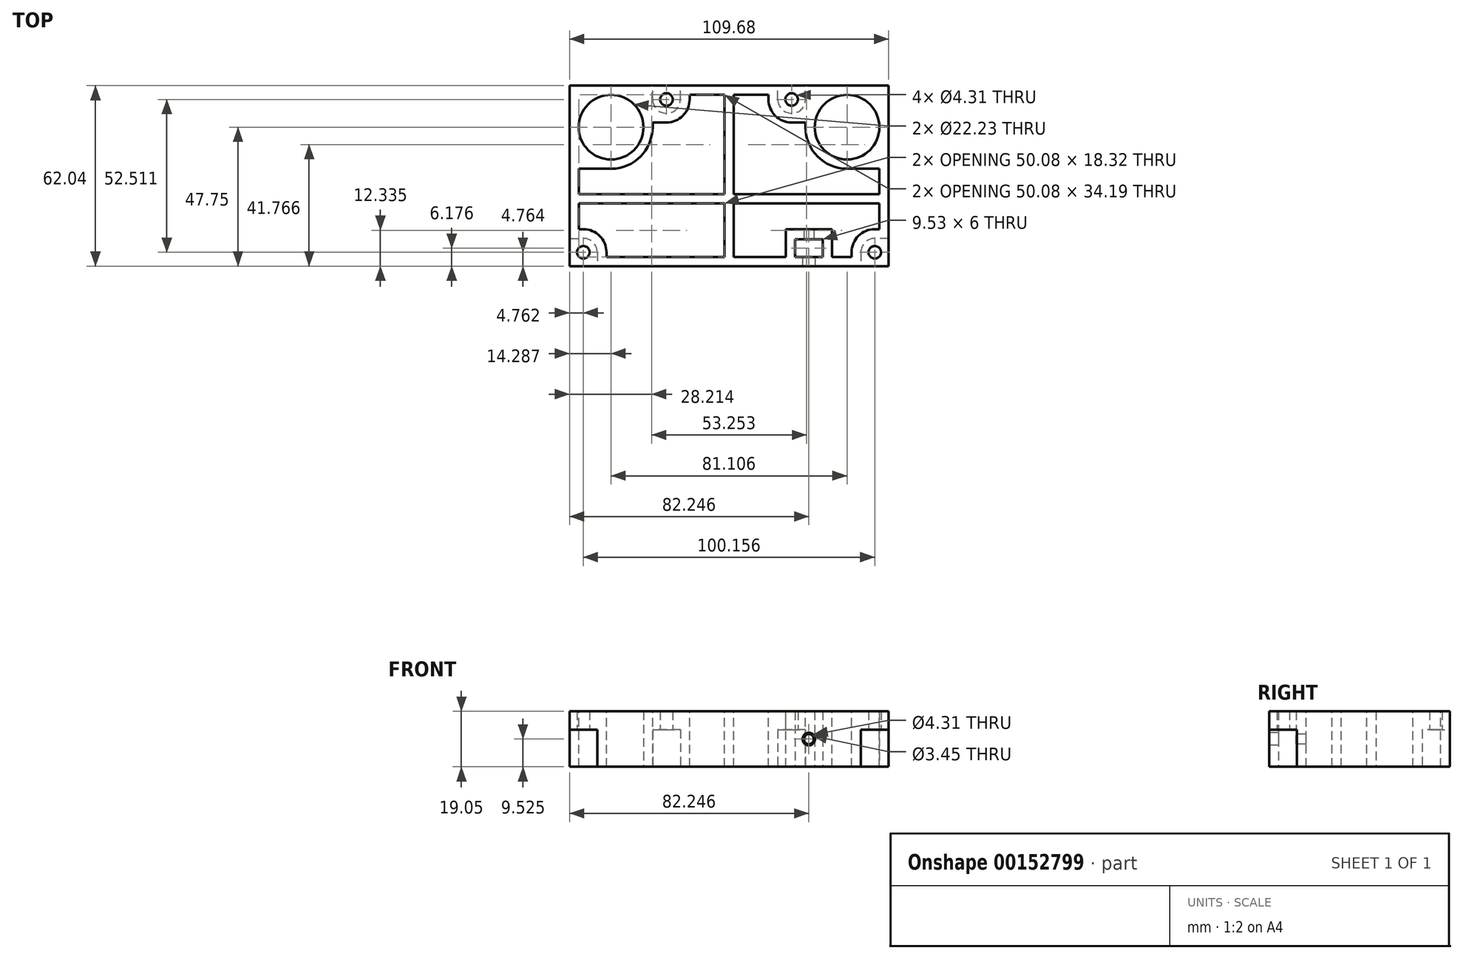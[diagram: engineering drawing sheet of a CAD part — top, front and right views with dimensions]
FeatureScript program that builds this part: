
annotation { "Feature Type Name" : "Feature", "Feature Type Description" : "" }
export const myFeature = defineFeature(function(context is Context, id is Id, definition is map)
    precondition{}
    {
        {
            var Q0;
            Q0=qCreatedBy(makeId("Top.planeOp"),FACE);
            var sketch = newSketch(context, id + "F0", { "sketchPlane" : qUnion([Q0])});
            skLineSegment(sketch, "E0.bottom", {"start": v(-40.55, 0) * mm, "end": v(40.55, 0) * mm, "construction": true});
            skPoint(sketch, "E0.middle", {"position": v(0, 0) * mm});
            skLineSegment(sketch, "E1", {"start": v(-40.55, 0) * mm, "end": v(-40.55, 14.29) * mm, "construction": true});
            skLineSegment(sketch, "E2", {"start": v(-40.55, 0) * mm, "end": v(-54.84, 0) * mm, "construction": true});
            skCircle(sketch, "E3", {"center": v(-40.55, 0) * mm, "radius": 11.11 * mm});
            skCircle(sketch, "E4", {"center": v(40.55, 0) * mm, "radius": 11.11 * mm});
            skLineSegment(sketch, "E5.bottom", {"start": v(-54.84, 14.29) * mm, "end": v(54.84, 14.29) * mm});
            skLineSegment(sketch, "E5.top", {"start": v(-54.84, -47.75) * mm, "end": v(54.84, -47.75) * mm});
            skLineSegment(sketch, "E5.left", {"start": v(-54.84, 14.29) * mm, "end": v(-54.84, -47.75) * mm});
            skLineSegment(sketch, "E5.right", {"start": v(54.84, 14.29) * mm, "end": v(54.84, -47.75) * mm});
            skLineSegment(sketch, "E6", {"start": v(0, 0) * mm, "end": v(0, -41.57) * mm, "construction": true});
            skLineSegment(sketch, "E7", {"start": v(0, -41.57) * mm, "end": v(22.64, -41.57) * mm, "construction": true});
            skLineSegment(sketch, "E8.bottom", {"start": v(22.64, -38.57) * mm, "end": v(32.17, -38.57) * mm});
            skLineSegment(sketch, "E8.top", {"start": v(22.64, -44.57) * mm, "end": v(32.17, -44.57) * mm});
            skLineSegment(sketch, "E8.left", {"start": v(22.64, -38.57) * mm, "end": v(22.64, -44.57) * mm});
            skLineSegment(sketch, "E8.right", {"start": v(32.17, -38.57) * mm, "end": v(32.17, -44.57) * mm});
            skLineSegment(sketch, "E9", {"start": v(0, -41.57) * mm, "end": v(0, -47.75) * mm, "construction": true});
            skLineSegment(sketch, "E10", {"start": v(0, 0) * mm, "end": v(0, 9.53) * mm, "construction": true});
            skLineSegment(sketch, "E11", {"start": v(-21.5, 9.53) * mm, "end": v(21.5, 9.53) * mm, "construction": true});
            skLineSegment(sketch, "E12", {"start": v(-50.08, -47.75) * mm, "end": v(-50.08, -42.99) * mm, "construction": true});
            skLineSegment(sketch, "E13", {"start": v(-50.08, -42.99) * mm, "end": v(-54.84, -42.99) * mm, "construction": true});
            skLineSegment(sketch, "E14", {"start": v(54.84, -42.99) * mm, "end": v(50.08, -42.99) * mm, "construction": true});
            skCircle(sketch, "E15", {"center": v(-50.08, -42.99) * mm, "radius": 2.15 * mm});
            skCircle(sketch, "E16", {"center": v(50.08, -42.99) * mm, "radius": 2.15 * mm});
            skCircle(sketch, "E17", {"center": v(-21.5, 9.53) * mm, "radius": 2.15 * mm});
            skCircle(sketch, "E18", {"center": v(21.5, 9.53) * mm, "radius": 2.15 * mm});
            skSolve(sketch);
        }
        {
            var Q0;
            Q0=qSketchRegion(id+"F0",true);
            extrude(context, id + "F1", {"entities" : qUnion([Q0]), "depth" : 19.05 * mm});
        }
        {
            var Q0;
            Q0=makeQuery(id+"F1.opExtrude","CAP_FACE",FACE,{"disambiguationData":[OSD([sQuery(id+"F0.wireOp",EDGE,"E3"),sQuery(id+"F0.wireOp",EDGE,"E4"),sQuery(id+"F0.wireOp",EDGE,"E5.bottom"),sQuery(id+"F0.wireOp",EDGE,"E5.top"),sQuery(id+"F0.wireOp",EDGE,"E5.left"),sQuery(id+"F0.wireOp",EDGE,"E5.right"),sQuery(id+"F0.wireOp",EDGE,"E8.bottom"),sQuery(id+"F0.wireOp",EDGE,"E8.top"),sQuery(id+"F0.wireOp",EDGE,"E8.left"),sQuery(id+"F0.wireOp",EDGE,"E8.right"),sQuery(id+"F0.wireOp",EDGE,"E15"),sQuery(id+"F0.wireOp",EDGE,"E16"),sQuery(id+"F0.wireOp",EDGE,"E17"),sQuery(id+"F0.wireOp",EDGE,"E18")])],"isStart":true});
            var sketch = newSketch(context, id + "F2", { "sketchPlane" : qUnion([Q0])});
            skLineSegment(sketch, "E19.bottom", {"start": v(-26.27, -14.29) * mm, "end": v(-16.74, -14.29) * mm});
            skLineSegment(sketch, "E19.top", {"start": v(-26.27, -4.76) * mm, "end": v(-16.74, -4.76) * mm});
            skLineSegment(sketch, "E19.left", {"start": v(-16.74, -4.76) * mm, "end": v(-16.74, -14.29) * mm});
            skLineSegment(sketch, "E19.right", {"start": v(-26.27, -4.76) * mm, "end": v(-26.27, -14.29) * mm});
            skPoint(sketch, "E19.middle", {"position": v(-21.5, -9.53) * mm});
            skLineSegment(sketch, "E20.bottom", {"start": v(26.27, -14.29) * mm, "end": v(16.74, -14.29) * mm});
            skLineSegment(sketch, "E20.top", {"start": v(26.27, -4.76) * mm, "end": v(16.74, -4.76) * mm});
            skLineSegment(sketch, "E20.left", {"start": v(16.74, -4.76) * mm, "end": v(16.74, -14.29) * mm});
            skLineSegment(sketch, "E20.right", {"start": v(26.27, -4.76) * mm, "end": v(26.27, -14.29) * mm});
            skPoint(sketch, "E20.middle", {"position": v(21.5, -9.53) * mm});
            skLineSegment(sketch, "E21.bottom", {"start": v(54.84, 47.75) * mm, "end": v(45.32, 47.75) * mm});
            skLineSegment(sketch, "E21.top", {"start": v(54.84, 38.22) * mm, "end": v(45.32, 38.22) * mm});
            skLineSegment(sketch, "E21.left", {"start": v(54.84, 38.22) * mm, "end": v(54.84, 47.75) * mm});
            skLineSegment(sketch, "E21.right", {"start": v(45.32, 38.22) * mm, "end": v(45.32, 47.75) * mm});
            skPoint(sketch, "E21.middle", {"position": v(50.08, 42.99) * mm});
            skLineSegment(sketch, "E22.bottom", {"start": v(-54.84, 47.75) * mm, "end": v(-45.32, 47.75) * mm});
            skLineSegment(sketch, "E22.top", {"start": v(-54.84, 38.22) * mm, "end": v(-45.32, 38.22) * mm});
            skLineSegment(sketch, "E22.left", {"start": v(-54.84, 38.22) * mm, "end": v(-54.84, 47.75) * mm});
            skLineSegment(sketch, "E22.right", {"start": v(-45.32, 38.22) * mm, "end": v(-45.32, 47.75) * mm});
            skPoint(sketch, "E22.middle", {"position": v(-50.08, 42.99) * mm});
            skSolve(sketch);
        }
        {
            var Q0;
            Q0=qSketchRegion(id+"F2",true);
            extrude(context, id + "F3", {"entities" : qUnion([Q0]), "operationType" : NewBodyOperationType.REMOVE, "oppositeDirection" : true, "depth" : 12.7 * mm});
        }
        {
            var Q0;
            Q0=makeQuery(id+"F3.boolean.opBoolean","COPY",EDGE,{"derivedFrom":makeQuery(id+"F3.opExtrude","SWEPT_EDGE",EDGE,{"disambiguationData":[OSD([sQuery(id+"F2.wireOp",EDGE,"E22.top"),sQuery(id+"F2.wireOp",EDGE,"E22.right")])]})});
            var Q1;
            Q1=makeQuery(id+"F3.boolean.opBoolean","COPY",EDGE,{"derivedFrom":makeQuery(id+"F3.opExtrude","SWEPT_EDGE",EDGE,{"disambiguationData":[OSD([sQuery(id+"F2.wireOp",EDGE,"E21.top"),sQuery(id+"F2.wireOp",EDGE,"E21.right")])]})});
            var Q2;
            Q2=makeQuery(id+"F3.boolean.opBoolean","COPY",EDGE,{"derivedFrom":makeQuery(id+"F3.opExtrude","SWEPT_EDGE",EDGE,{"disambiguationData":[OSD([sQuery(id+"F2.wireOp",EDGE,"E20.top"),sQuery(id+"F2.wireOp",EDGE,"E20.right")])]})});
            var Q3;
            Q3=makeQuery(id+"F3.boolean.opBoolean","COPY",EDGE,{"derivedFrom":makeQuery(id+"F3.opExtrude","SWEPT_EDGE",EDGE,{"disambiguationData":[OSD([sQuery(id+"F2.wireOp",EDGE,"E20.top"),sQuery(id+"F2.wireOp",EDGE,"E20.left")])]})});
            var Q4;
            Q4=makeQuery(id+"F3.boolean.opBoolean","COPY",EDGE,{"derivedFrom":makeQuery(id+"F3.opExtrude","SWEPT_EDGE",EDGE,{"disambiguationData":[OSD([sQuery(id+"F2.wireOp",EDGE,"E19.top"),sQuery(id+"F2.wireOp",EDGE,"E19.right")])]})});
            var Q5;
            Q5=makeQuery(id+"F3.boolean.opBoolean","COPY",EDGE,{"derivedFrom":makeQuery(id+"F3.opExtrude","SWEPT_EDGE",EDGE,{"disambiguationData":[OSD([sQuery(id+"F2.wireOp",EDGE,"E19.top"),sQuery(id+"F2.wireOp",EDGE,"E19.left")])]})});
            fillet(context, id + "F4", {"entities" : qUnion([Q0, Q1, Q2, Q3, Q4, Q5]), "radius" : 4.76 * mm, "tangentPropagation" : true, "allowEdgeOverflow" : false});
        }
        {
            var Q0;
            Q0=makeQuery(id+"F1.opExtrude","CAP_FACE",FACE,{"disambiguationData":[OSD([sQuery(id+"F0.wireOp",EDGE,"E3"),sQuery(id+"F0.wireOp",EDGE,"E4"),sQuery(id+"F0.wireOp",EDGE,"E5.bottom"),sQuery(id+"F0.wireOp",EDGE,"E5.top"),sQuery(id+"F0.wireOp",EDGE,"E5.left"),sQuery(id+"F0.wireOp",EDGE,"E5.right"),sQuery(id+"F0.wireOp",EDGE,"E8.bottom"),sQuery(id+"F0.wireOp",EDGE,"E8.top"),sQuery(id+"F0.wireOp",EDGE,"E8.left"),sQuery(id+"F0.wireOp",EDGE,"E8.right"),sQuery(id+"F0.wireOp",EDGE,"E15"),sQuery(id+"F0.wireOp",EDGE,"E16"),sQuery(id+"F0.wireOp",EDGE,"E17"),sQuery(id+"F0.wireOp",EDGE,"E18")])],"isStart":false});
            var sketch = newSketch(context, id + "F5", { "sketchPlane" : qUnion([Q0])});
            skLineSegment(sketch, "E23.bottom", {"start": v(51.67, -23.08) * mm, "end": v(-51.67, -23.08) * mm});
            skLineSegment(sketch, "E23.top", {"start": v(51.67, -26.26) * mm, "end": v(-51.67, -26.26) * mm});
            skLineSegment(sketch, "E23.left", {"start": v(51.67, -23.08) * mm, "end": v(51.67, -26.26) * mm, "construction": true});
            skLineSegment(sketch, "E23.right", {"start": v(-51.67, -23.08) * mm, "end": v(-51.67, -26.26) * mm, "construction": true});
            skLineSegment(sketch, "E24.bottom", {"start": v(-1.59, -44.57) * mm, "end": v(1.59, -44.57) * mm, "construction": true});
            skLineSegment(sketch, "E24.top", {"start": v(-1.59, 11.11) * mm, "end": v(1.59, 11.11) * mm, "construction": true});
            skLineSegment(sketch, "E24.left", {"start": v(-1.59, -44.57) * mm, "end": v(-1.59, 11.11) * mm});
            skLineSegment(sketch, "E24.right", {"start": v(1.59, -44.57) * mm, "end": v(1.59, 11.11) * mm});
            skArc(sketch, "E25", {"start": v(-40.55, -14.29) * mm, "mid": v(-30.45, -10.1) * mm, "end": v(-26.27, 0) * mm});
            skArc(sketch, "E26", {"start": v(-21.5, 1.59) * mm, "mid": v(-15.9, 3.91) * mm, "end": v(-13.57, 9.53) * mm});
            skArc(sketch, "E27", {"start": v(13.57, 9.53) * mm, "mid": v(15.9, 3.91) * mm, "end": v(21.5, 1.59) * mm});
            skArc(sketch, "E28", {"start": v(26.27, 0) * mm, "mid": v(30.45, -10.1) * mm, "end": v(40.55, -14.29) * mm});
            skArc(sketch, "E29", {"start": v(50.08, -35.05) * mm, "mid": v(44.47, -37.37) * mm, "end": v(42.14, -42.99) * mm});
            skArc(sketch, "E30", {"start": v(-42.14, -42.99) * mm, "mid": v(-44.47, -37.37) * mm, "end": v(-50.08, -35.05) * mm});
            skLineSegment(sketch, "E31", {"start": v(27.4, -44.57) * mm, "end": v(27.4, -47.75) * mm, "construction": true});
            skLineSegment(sketch, "E32", {"start": v(27.4, -44.57) * mm, "end": v(27.4, -35.05) * mm, "construction": true});
            skLineSegment(sketch, "E33.bottom", {"start": v(19.47, -35.05) * mm, "end": v(35.34, -35.05) * mm});
            skLineSegment(sketch, "E33.left", {"start": v(19.47, -35.05) * mm, "end": v(19.47, -44.57) * mm});
            skLineSegment(sketch, "E33.right", {"start": v(35.34, -35.05) * mm, "end": v(35.34, -44.57) * mm});
            skLineSegment(sketch, "E34", {"start": v(22.64, -38.57) * mm, "end": v(19.47, -38.57) * mm, "construction": true});
            skLineSegment(sketch, "E35", {"start": v(19.47, -44.57) * mm, "end": v(1.59, -44.57) * mm});
            skLineSegment(sketch, "E36", {"start": v(35.34, -44.57) * mm, "end": v(42.14, -44.57) * mm});
            skLineSegment(sketch, "E37", {"start": v(42.14, -44.57) * mm, "end": v(42.14, -42.99) * mm});
            skLineSegment(sketch, "E38", {"start": v(-1.59, -44.57) * mm, "end": v(-42.14, -44.57) * mm});
            skLineSegment(sketch, "E39", {"start": v(0, -44.57) * mm, "end": v(0, -47.75) * mm, "construction": true});
            skLineSegment(sketch, "E40", {"start": v(-42.14, -44.57) * mm, "end": v(-42.14, -42.99) * mm});
            skLineSegment(sketch, "E41", {"start": v(-40.55, -14.29) * mm, "end": v(-51.67, -14.29) * mm});
            skLineSegment(sketch, "E42", {"start": v(-51.67, -14.29) * mm, "end": v(-51.67, -23.08) * mm});
            skLineSegment(sketch, "E43", {"start": v(-50.08, -35.05) * mm, "end": v(-51.67, -35.05) * mm});
            skLineSegment(sketch, "E44", {"start": v(-51.67, -35.05) * mm, "end": v(-51.67, -26.26) * mm});
            skLineSegment(sketch, "E45", {"start": v(-51.67, -14.29) * mm, "end": v(-54.84, -14.29) * mm, "construction": true});
            skLineSegment(sketch, "E46", {"start": v(-26.27, 0) * mm, "end": v(-26.27, 1.59) * mm});
            skLineSegment(sketch, "E47", {"start": v(-26.27, 1.59) * mm, "end": v(-21.5, 1.59) * mm});
            skLineSegment(sketch, "E48", {"start": v(50.08, -35.05) * mm, "end": v(51.67, -35.05) * mm});
            skLineSegment(sketch, "E49", {"start": v(51.67, -35.05) * mm, "end": v(51.67, -26.26) * mm});
            skLineSegment(sketch, "E50", {"start": v(51.67, -23.08) * mm, "end": v(51.67, -14.29) * mm});
            skLineSegment(sketch, "E51", {"start": v(51.67, -14.29) * mm, "end": v(40.55, -14.29) * mm});
            skLineSegment(sketch, "E52", {"start": v(26.27, 0) * mm, "end": v(26.27, 1.59) * mm});
            skLineSegment(sketch, "E53", {"start": v(26.27, 1.59) * mm, "end": v(21.5, 1.59) * mm});
            skLineSegment(sketch, "E54", {"start": v(-13.57, 9.53) * mm, "end": v(-13.57, 11.11) * mm});
            skLineSegment(sketch, "E55", {"start": v(-13.57, 11.11) * mm, "end": v(-1.59, 11.11) * mm});
            skLineSegment(sketch, "E56", {"start": v(13.57, 9.53) * mm, "end": v(13.57, 11.11) * mm});
            skLineSegment(sketch, "E57", {"start": v(13.57, 11.11) * mm, "end": v(1.59, 11.11) * mm});
            skLineSegment(sketch, "E58", {"start": v(0, 11.11) * mm, "end": v(0, 14.29) * mm, "construction": true});
            skLineSegment(sketch, "E59", {"start": v(51.67, -24.67) * mm, "end": v(54.84, -24.67) * mm, "construction": true});
            skSolve(sketch);
        }
        {
            var Q0;
            Q0=makeQuery(id+"F5.imprint","IMPRINT",FACE,{"disambiguationData":[TD([[makeQuery(id+"F5.imprint","IMPRINT",EDGE,{"derivedFrom":sQuery(id+"F5.wireOp",EDGE,"E25")}),-1.0]])]});
            var Q1;
            Q1=makeQuery(id+"F5.imprint","IMPRINT",FACE,{"disambiguationData":[TD([[makeQuery(id+"F5.imprint","IMPRINT",EDGE,{"derivedFrom":sQuery(id+"F5.wireOp",EDGE,"E30")}),-1.0]])]});
            var Q2;
            Q2=makeQuery(id+"F5.imprint","IMPRINT",FACE,{"disambiguationData":[TD([[makeQuery(id+"F5.imprint","IMPRINT",EDGE,{"derivedFrom":sQuery(id+"F5.wireOp",EDGE,"E27")}),-1.0]])]});
            var Q3;
            Q3=makeQuery(id+"F5.imprint","IMPRINT",FACE,{"disambiguationData":[TD([[makeQuery(id+"F5.imprint","IMPRINT",EDGE,{"derivedFrom":sQuery(id+"F5.wireOp",EDGE,"E29")}),-1.0]])]});
            var Q4;
            Q4=makeQuery(id+"F1.opExtrude","CAP_FACE",FACE,{"disambiguationData":[OSD([sQuery(id+"F0.wireOp",EDGE,"E3"),sQuery(id+"F0.wireOp",EDGE,"E4"),sQuery(id+"F0.wireOp",EDGE,"E5.bottom"),sQuery(id+"F0.wireOp",EDGE,"E5.top"),sQuery(id+"F0.wireOp",EDGE,"E5.left"),sQuery(id+"F0.wireOp",EDGE,"E5.right"),sQuery(id+"F0.wireOp",EDGE,"E8.bottom"),sQuery(id+"F0.wireOp",EDGE,"E8.top"),sQuery(id+"F0.wireOp",EDGE,"E8.left"),sQuery(id+"F0.wireOp",EDGE,"E8.right"),sQuery(id+"F0.wireOp",EDGE,"E15"),sQuery(id+"F0.wireOp",EDGE,"E16"),sQuery(id+"F0.wireOp",EDGE,"E17"),sQuery(id+"F0.wireOp",EDGE,"E18")])],"isStart":true});
            extrude(context, id + "F6", {"entities" : qUnion([Q0, Q1, Q2, Q3]), "operationType" : NewBodyOperationType.REMOVE, "endBound" : BoundingType.UP_TO_SURFACE, "oppositeDirection" : true, "endBoundEntityFace" : qUnion([Q4]), "depth" : 25.4 * mm});
        }
        {
            var Q0;
            Q0=makeQuery(id+"F1.opExtrude","SWEPT_FACE",FACE,{"disambiguationData":[OSD([sQuery(id+"F0.wireOp",EDGE,"E5.top")])]});
            var sketch = newSketch(context, id + "F7", { "sketchPlane" : qUnion([Q0])});
            skLineSegment(sketch, "E60", {"start": v(27.4, 19.05) * mm, "end": v(27.4, 0) * mm, "construction": true});
            skCircle(sketch, "E61", {"center": v(27.4, 9.53) * mm, "radius": 2.15 * mm});
            skSolve(sketch);
        }
        {
            var Q0;
            Q0=qSketchRegion(id+"F7",true);
            var Q1;
            Q1=makeQuery(id+"F1.opExtrude","SWEPT_FACE",FACE,{"disambiguationData":[OSD([sQuery(id+"F0.wireOp",EDGE,"E8.top")])]});
            extrude(context, id + "F8", {"entities" : qUnion([Q0]), "operationType" : NewBodyOperationType.REMOVE, "endBound" : BoundingType.UP_TO_SURFACE, "oppositeDirection" : true, "endBoundEntityFace" : qUnion([Q1]), "depth" : 25.4 * mm});
        }
        {
            var Q0;
            Q0=makeQuery(id+"F1.opExtrude","SWEPT_FACE",FACE,{"disambiguationData":[OSD([sQuery(id+"F0.wireOp",EDGE,"E8.bottom")])]});
            var sketch = newSketch(context, id + "F9", { "sketchPlane" : qUnion([Q0])});
            skCircle(sketch, "E62", {"center": v(27.4, 9.53) * mm, "radius": 1.73 * mm});
            skSolve(sketch);
        }
        {
            var Q0;
            Q0=qSketchRegion(id+"F9",true);
            var Q1;
            Q1=makeQuery(id+"F6.boolean.opBoolean","COPY",FACE,{"derivedFrom":makeQuery(id+"F6.opExtrude","SWEPT_FACE",FACE,{"disambiguationData":[OSD([sQuery(id+"F5.wireOp",EDGE,"E33.bottom")])]})});
            extrude(context, id + "F10", {"entities" : qUnion([Q0]), "operationType" : NewBodyOperationType.REMOVE, "endBound" : BoundingType.UP_TO_SURFACE, "oppositeDirection" : true, "endBoundEntityFace" : qUnion([Q1]), "depth" : 25.4 * mm});
        }
    });
